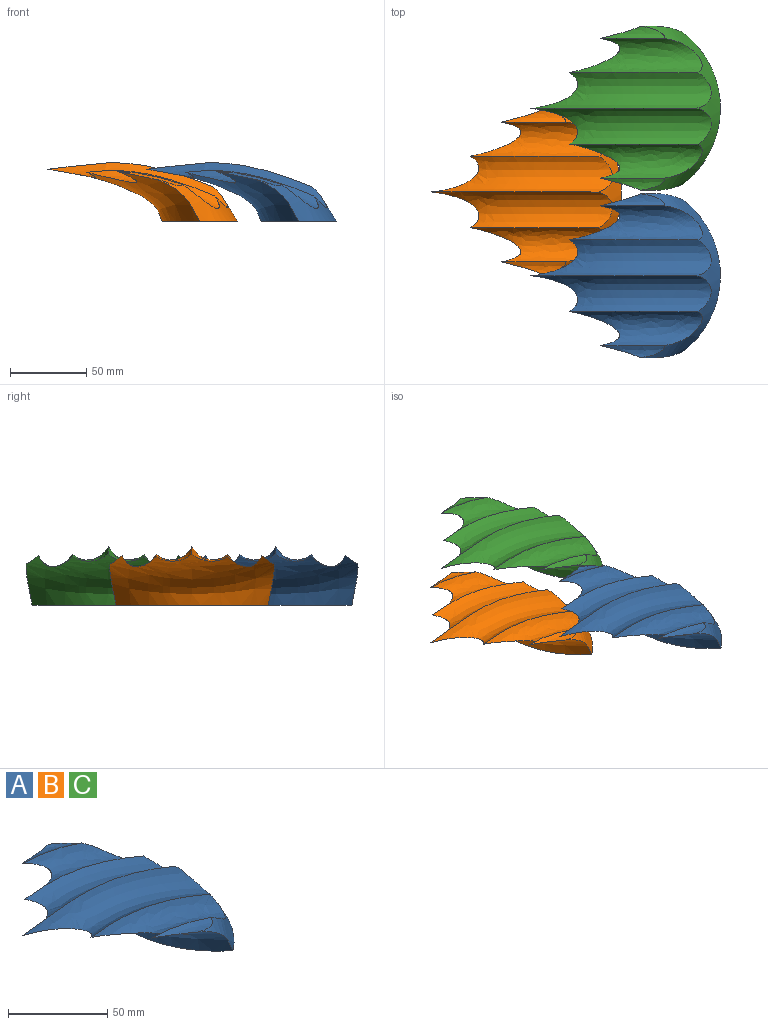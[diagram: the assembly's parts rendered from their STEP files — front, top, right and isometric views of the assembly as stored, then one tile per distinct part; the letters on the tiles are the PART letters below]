
ASSEMBLY  parts=3 mates=2
PART A: 9 faces, bbox 148.3x118.6x56.8 mm
  f0: plane 100x49.44mm, normal (0,0,-1), area 3452.1mm2, adj f1,f2
  f1: bspline ~108.61x78.21mm, area 1892.3mm2, adj f0,f2,f3,f4,f5,f6,f7,f8
  f2: bspline ~108.61x100mm, area 6122.4mm2, adj f0,f1,f3,f4,f5,f6,f7,f8
  f3: bspline ~82.66x28.18mm, area 208.5mm2, adj f1,f2,f5
  f4: bspline ~82.66x28.18mm, area 208.3mm2, adj f1,f2,f8
  f5: offset ~139.21x51.9mm, area 1673.1mm2, adj f1,f2,f3,f6
  f6: bspline ~138.32x41.78mm, area 2663.5mm2, adj f1,f2,f5,f7
  f7: bspline ~138.32x41.78mm, area 2663.5mm2, adj f1,f2,f6,f8
  f8: offset ~139.21x51.9mm, area 1672.5mm2, adj f1,f2,f4,f7
PART B: same geometry as A
PART C: same geometry as A
PLACE A at identity
PLACE B t=(-65,55,0)mm
PLACE C t=(0,110,0)mm
MATE fastened B.f0 <-> A.f0  axis (0,0,-1) through (-65,55,0)mm
MATE fastened A.f0 <-> C.f0  axis (0,0,-1) through (0,0,0)mm
